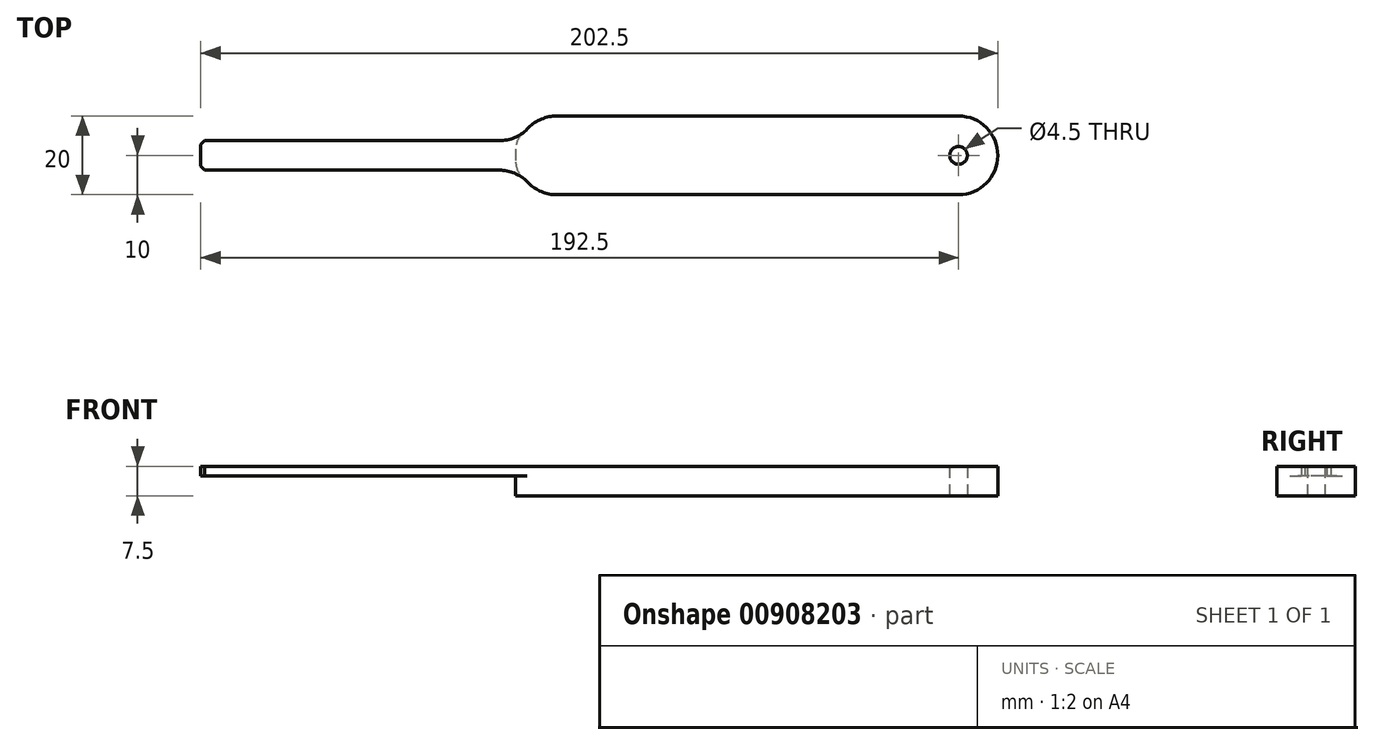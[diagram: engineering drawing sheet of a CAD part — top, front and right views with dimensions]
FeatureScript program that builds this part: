
annotation { "Feature Type Name" : "Feature", "Feature Type Description" : "" }
export const myFeature = defineFeature(function(context is Context, id is Id, definition is map)
    precondition{}
    {
        {
            var Q0;
            Q0=qCreatedBy(makeId("Top.planeOp"),FACE);
            var sketch = newSketch(context, id + "F0", { "sketchPlane" : qUnion([Q0])});
            skLineSegment(sketch, "E0.bottom", {"start": v(-40, 3.75) * mm, "end": v(40, 3.75) * mm});
            skLineSegment(sketch, "E0.top", {"start": v(-40, -3.75) * mm, "end": v(40, -3.75) * mm});
            skLineSegment(sketch, "E0.left", {"start": v(-40, 3.75) * mm, "end": v(-40, -3.75) * mm});
            skLineSegment(sketch, "E0.right", {"start": v(40, 3.75) * mm, "end": v(40, -3.75) * mm});
            skPoint(sketch, "E0.middle", {"position": v(0, 0) * mm});
            skLineSegment(sketch, "E1", {"start": v(-40, 0) * mm, "end": v(0, 0) * mm, "construction": true});
            skLineSegment(sketch, "E2", {"start": v(40, 3.75) * mm, "end": v(46.25, 10) * mm});
            skLineSegment(sketch, "E3", {"start": v(46.25, 10) * mm, "end": v(152.5, 10) * mm});
            skLineSegment(sketch, "E4", {"start": v(40, 0) * mm, "end": v(311.31, 0) * mm, "construction": true});
            skLineSegment(sketch, "E5", {"start": v(152.5, -10) * mm, "end": v(46.25, -10) * mm});
            skLineSegment(sketch, "E6", {"start": v(46.25, -10) * mm, "end": v(40, -3.75) * mm});
            skCircle(sketch, "E7", {"center": v(152.5, 0) * mm, "radius": 2.25 * mm});
            skArc(sketch, "E8", {"start": v(152.5, 10) * mm, "mid": v(162.5, 0) * mm, "end": v(152.5, -10) * mm});
            skSolve(sketch);
        }
        {
            var Q0;
            Q0 = qSketchRegion(id + "F0", true);
            extrude(context, id + "F1", {"entities" : qUnion([Q0]), "depth" : 2.5 * mm, "offsetDistance" : 25 * mm});
        }
        {
            var Q0;
            Q0=makeQuery(id+"F0.imprint","IMPRINT",FACE,{"disambiguationData":[TD([[makeQuery(id+"F0.imprint","IMPRINT",EDGE,{"derivedFrom":sQuery(id+"F0.wireOp",EDGE,"E0.right")}),1.0]])]});
            extrude(context, id + "F2", {"entities" : qUnion([Q0]), "operationType" : NewBodyOperationType.ADD, "oppositeDirection" : true, "depth" : 5 * mm, "offsetDistance" : 25 * mm});
        }
        {
            var Q0;
            Q0=makeQuery(id+"F1.opExtrude","SWEPT_EDGE",EDGE,{"disambiguationData":[OSD([sQuery(id+"F0.wireOp",EDGE,"E0.top"),sQuery(id+"F0.wireOp",EDGE,"E0.left")])]});
            var Q1;
            Q1=makeQuery(id+"F1.opExtrude","SWEPT_EDGE",EDGE,{"disambiguationData":[OSD([sQuery(id+"F0.wireOp",EDGE,"E0.bottom"),sQuery(id+"F0.wireOp",EDGE,"E0.left")])]});
            chamfer(context, id + "F3", {"entities" : qUnion([Q0, Q1]), "width" : 1 * mm, "tangentPropagation" : true});
        }
        {
            var Q0;
            Q0=makeQuery(id+"F1.opExtrude","SWEPT_EDGE",EDGE,{"disambiguationData":[OSD([sQuery(id+"F0.wireOp",EDGE,"E0.top"),sQuery(id+"F0.wireOp",EDGE,"E0.right"),sQuery(id+"F0.wireOp",EDGE,"E6")])]});
            var Q1;
            {var subQ0=sQuery(id+"F0.wireOp",EDGE,"E6");var subQ1=sQuery(id+"F0.wireOp",EDGE,"E5");Q1=makeQuery(id+"F2.boolean.opBoolean","MERGE",EDGE,{"derivedFrom":[makeQuery(id+"F1.opExtrude","SWEPT_EDGE",EDGE,{"disambiguationData":[OSD([subQ1,subQ0])]}),makeQuery(id+"F2.opExtrude","SWEPT_EDGE",EDGE,{"disambiguationData":[OSD([subQ1,subQ0])]})]});}
            var Q2;
            {var subQ0=sQuery(id+"F0.wireOp",EDGE,"E3");var subQ1=sQuery(id+"F0.wireOp",EDGE,"E2");Q2=makeQuery(id+"F2.boolean.opBoolean","MERGE",EDGE,{"derivedFrom":[makeQuery(id+"F1.opExtrude","SWEPT_EDGE",EDGE,{"disambiguationData":[OSD([subQ1,subQ0])]}),makeQuery(id+"F2.opExtrude","SWEPT_EDGE",EDGE,{"disambiguationData":[OSD([subQ1,subQ0])]})]});}
            var Q3;
            Q3=makeQuery(id+"F1.opExtrude","SWEPT_EDGE",EDGE,{"disambiguationData":[OSD([sQuery(id+"F0.wireOp",EDGE,"E0.bottom"),sQuery(id+"F0.wireOp",EDGE,"E0.right"),sQuery(id+"F0.wireOp",EDGE,"E2")])]});
            fillet(context, id + "F4", {"entities" : qUnion([Q0, Q1, Q2, Q3]), "tangentPropagation" : true, "radius" : 10 * mm, "defaultsChanged" : true, "vertexSettings" : [], "allowEdgeOverflow" : false});
        }
        {
            var Q0;
            Q0=makeQuery(id+"F2.opExtrude","SWEPT_EDGE",EDGE,{"disambiguationData":[OSD([sQuery(id+"F0.wireOp",EDGE,"E0.top"),sQuery(id+"F0.wireOp",EDGE,"E0.right"),sQuery(id+"F0.wireOp",EDGE,"E6")])]});
            var Q1;
            Q1=makeQuery(id+"F2.opExtrude","SWEPT_EDGE",EDGE,{"disambiguationData":[OSD([sQuery(id+"F0.wireOp",EDGE,"E0.bottom"),sQuery(id+"F0.wireOp",EDGE,"E0.right"),sQuery(id+"F0.wireOp",EDGE,"E2")])]});
            fillet(context, id + "F5", {"entities" : qUnion([Q0, Q1]), "tangentPropagation" : true, "radius" : 5 * mm, "defaultsChanged" : false, "vertexSettings" : [], "allowEdgeOverflow" : false});
        }
    });
